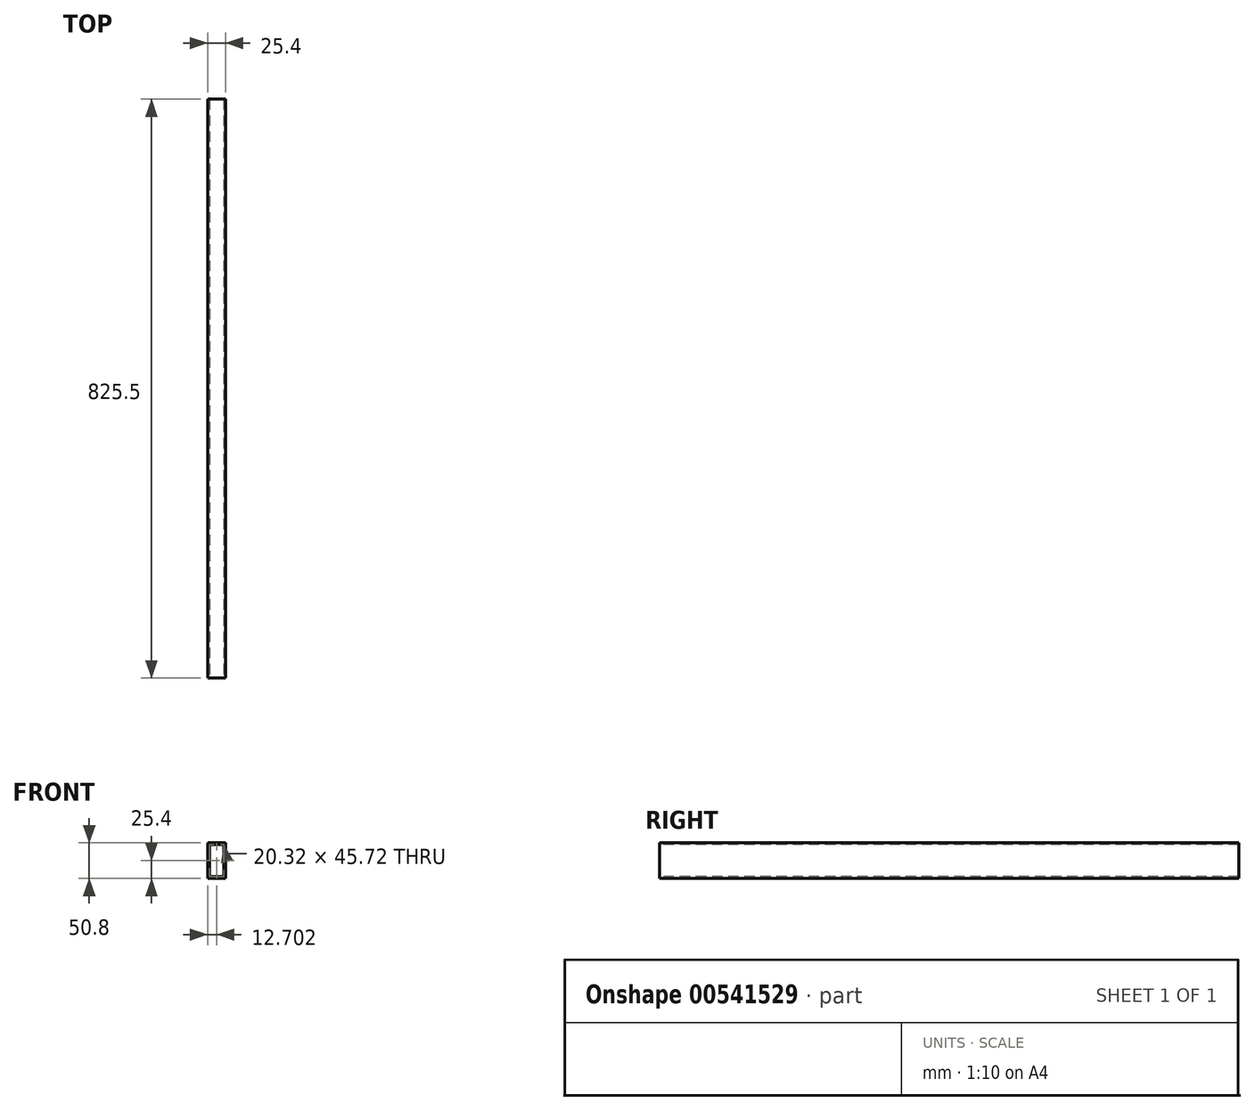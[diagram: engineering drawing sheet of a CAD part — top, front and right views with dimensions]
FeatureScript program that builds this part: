
annotation { "Feature Type Name" : "Feature", "Feature Type Description" : "" }
export const myFeature = defineFeature(function(context is Context, id is Id, definition is map)
    precondition{}
    {
        {
            var Q0;
            Q0=qCreatedBy(makeId("Front.planeOp"),FACE);
            var sketch = newSketch(context, id + "F0", { "sketchPlane" : qUnion([Q0])});
            skLineSegment(sketch, "E0.bottom", {"start": v(-6.42, 41.8) * mm, "end": v(18.98, 41.8) * mm});
            skLineSegment(sketch, "E0.top", {"start": v(-6.42, -9) * mm, "end": v(18.98, -9) * mm});
            skLineSegment(sketch, "E0.left", {"start": v(-6.42, 41.8) * mm, "end": v(-6.42, -9) * mm});
            skLineSegment(sketch, "E0.right", {"start": v(18.98, 41.8) * mm, "end": v(18.98, -9) * mm});
            skSolve(sketch);
        }
        {
            var Q0;
            Q0=makeQuery(id+"F0.imprint","IMPRINT",FACE,{"disambiguationData":[TD([[makeQuery(id+"F0.imprint","IMPRINT",EDGE,{"derivedFrom":sQuery(id+"F0.wireOp",EDGE,"E0.bottom")}),-1.0]])]});
            extrude(context, id + "F1", {"entities" : qUnion([Q0]), "depth" : 825.5 * mm, "offsetDistance" : 25.4 * mm});
        }
        {
            var Q0;
            Q0=makeQuery(id+"F1.opExtrude","CAP_FACE",FACE,{"disambiguationData":[OSD([sQuery(id+"F0.wireOp",EDGE,"E0.bottom"),sQuery(id+"F0.wireOp",EDGE,"E0.top"),sQuery(id+"F0.wireOp",EDGE,"E0.left"),sQuery(id+"F0.wireOp",EDGE,"E0.right")])],"isStart":false});
            var sketch = newSketch(context, id + "F2", { "sketchPlane" : qUnion([Q0])});
            skLineSegment(sketch, "E1.bottom", {"start": v(-3.88, 39.25) * mm, "end": v(16.44, 39.25) * mm});
            skLineSegment(sketch, "E1.top", {"start": v(-3.88, -6.47) * mm, "end": v(16.44, -6.47) * mm});
            skLineSegment(sketch, "E1.left", {"start": v(-3.88, 39.25) * mm, "end": v(-3.88, -6.47) * mm});
            skLineSegment(sketch, "E1.right", {"start": v(16.44, 39.25) * mm, "end": v(16.44, -6.47) * mm});
            skSolve(sketch);
        }
        {
            var Q0;
            Q0=qSketchRegion(id+"F2",true);
            extrude(context, id + "F3", {"entities" : qUnion([Q0]), "operationType" : NewBodyOperationType.REMOVE, "endBound" : BoundingType.THROUGH_ALL, "oppositeDirection" : true, "depth" : 25.4 * mm, "offsetDistance" : 25.4 * mm});
        }
    });
